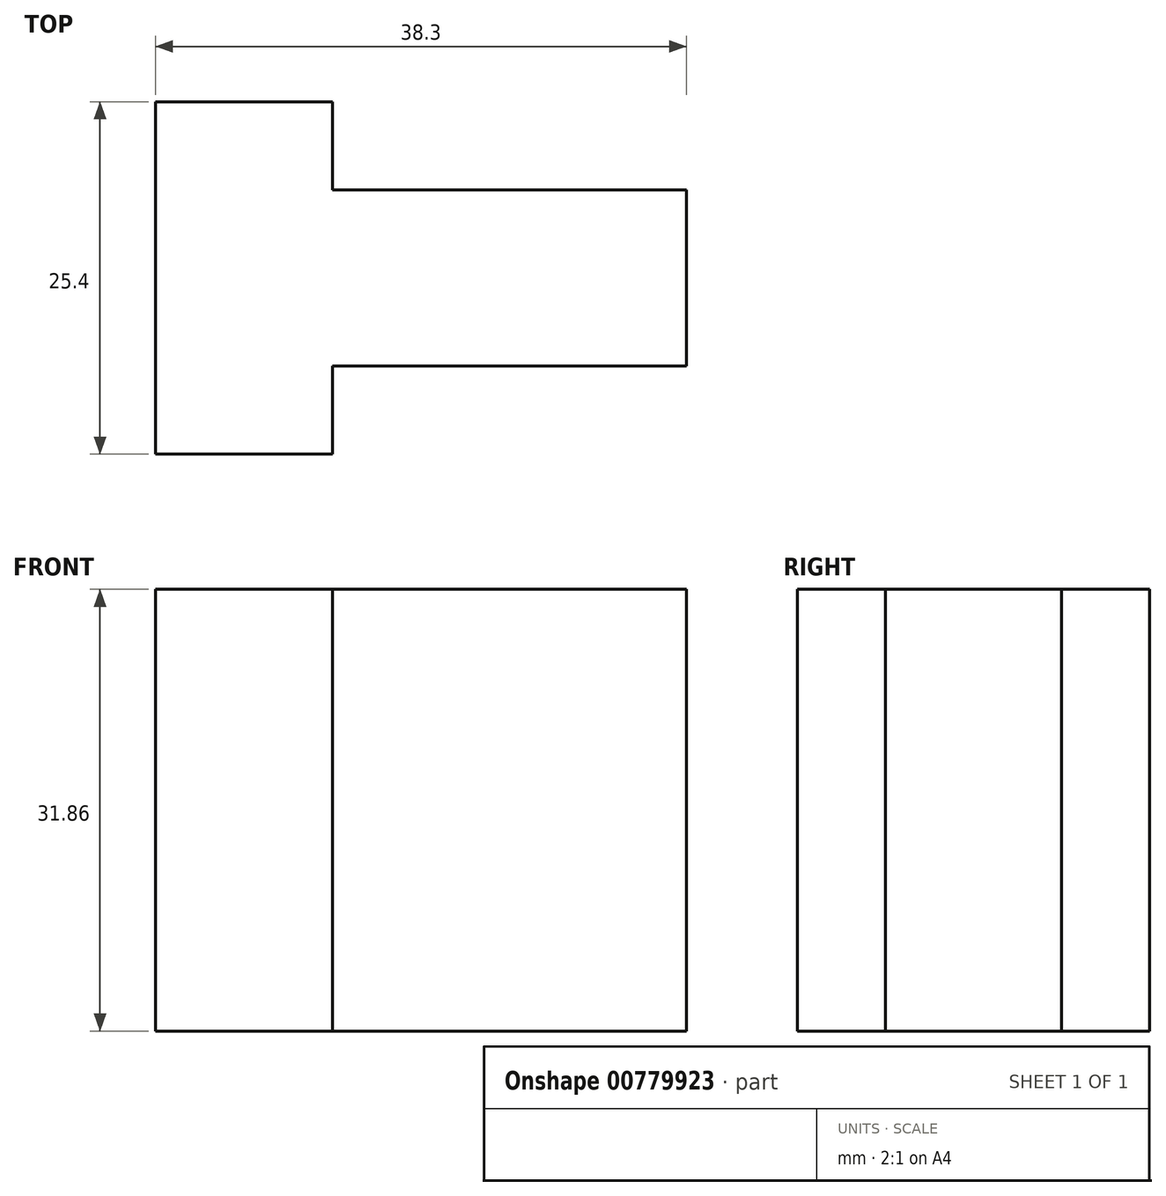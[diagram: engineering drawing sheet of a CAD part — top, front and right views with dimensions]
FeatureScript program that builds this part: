
annotation { "Feature Type Name" : "Feature", "Feature Type Description" : "" }
export const myFeature = defineFeature(function(context is Context, id is Id, definition is map)
    precondition{}
    {
        {
            var Q0;
            Q0=qCreatedBy(makeId("Front.planeOp"),FACE);
            var sketch = newSketch(context, id + "F0", { "sketchPlane" : qUnion([Q0])});
            skLineSegment(sketch, "E0", {"start": v(0, 0) * mm, "end": v(38.3, 0) * mm});
            skLineSegment(sketch, "E1", {"start": v(38.3, 0) * mm, "end": v(38.3, 31.86) * mm});
            skLineSegment(sketch, "E2", {"start": v(38.3, 31.86) * mm, "end": v(0, 31.86) * mm});
            skLineSegment(sketch, "E3", {"start": v(0, 31.86) * mm, "end": v(0, 0) * mm});
            skSolve(sketch);
        }
        {
            var Q0;
            Q0 = qSketchRegion(id + "F0", true);
            extrude(context, id + "F1", {"entities" : qUnion([Q0]), "depth" : 25.4 * mm, "offsetDistance" : 25.4 * mm});
        }
        {
            var Q0;
            Q0=makeQuery(id+"F1.opExtrude","CAP_FACE",FACE,{"disambiguationData":[OSD([sQuery(id+"F0.wireOp",EDGE,"E0"),sQuery(id+"F0.wireOp",EDGE,"E1"),sQuery(id+"F0.wireOp",EDGE,"E2"),sQuery(id+"F0.wireOp",EDGE,"E3")])],"isStart":false});
            var sketch = newSketch(context, id + "F2", { "sketchPlane" : qUnion([Q0])});
            skLineSegment(sketch, "E4", {"start": v(0, 31.86) * mm, "end": v(12.77, 31.86) * mm});
            skLineSegment(sketch, "E5", {"start": v(12.77, 31.86) * mm, "end": v(12.77, 0) * mm});
            skSolve(sketch);
        }
        {
            var Q0;
            {var subQ0=sQuery(id+"F2.wireOp",EDGE,"E5");Q0=makeQuery(id+"F2.imprint","IMPRINT",FACE,{"disambiguationData":[TD([[makeQuery(id+"F2.imprint","IMPRINT",EDGE,{"derivedFrom":subQ0}),1.0]])]});}
            extrude(context, id + "F3", {"entities" : qUnion([Q0]), "operationType" : NewBodyOperationType.REMOVE, "oppositeDirection" : true, "depth" : 6.35 * mm, "offsetDistance" : 25.4 * mm});
        }
        {
            var Q0;
            Q0=makeQuery(id+"F1.opExtrude","CAP_FACE",FACE,{"disambiguationData":[OSD([sQuery(id+"F0.wireOp",EDGE,"E0"),sQuery(id+"F0.wireOp",EDGE,"E1"),sQuery(id+"F0.wireOp",EDGE,"E2"),sQuery(id+"F0.wireOp",EDGE,"E3")])],"isStart":true});
            var sketch = newSketch(context, id + "F4", { "sketchPlane" : qUnion([Q0])});
            skLineSegment(sketch, "E6", {"start": v(0, 31.86) * mm, "end": v(-12.77, 31.86) * mm});
            skLineSegment(sketch, "E7", {"start": v(-12.77, 31.86) * mm, "end": v(-12.77, 0) * mm});
            skSolve(sketch);
        }
        {
            var Q0;
            {var subQ0=sQuery(id+"F4.wireOp",EDGE,"E7");Q0=makeQuery(id+"F4.imprint","IMPRINT",FACE,{"disambiguationData":[TD([[makeQuery(id+"F4.imprint","IMPRINT",EDGE,{"derivedFrom":subQ0}),-1.0]])]});}
            extrude(context, id + "F5", {"entities" : qUnion([Q0]), "operationType" : NewBodyOperationType.REMOVE, "oppositeDirection" : true, "depth" : 6.35 * mm, "offsetDistance" : 25.4 * mm});
        }
    });
